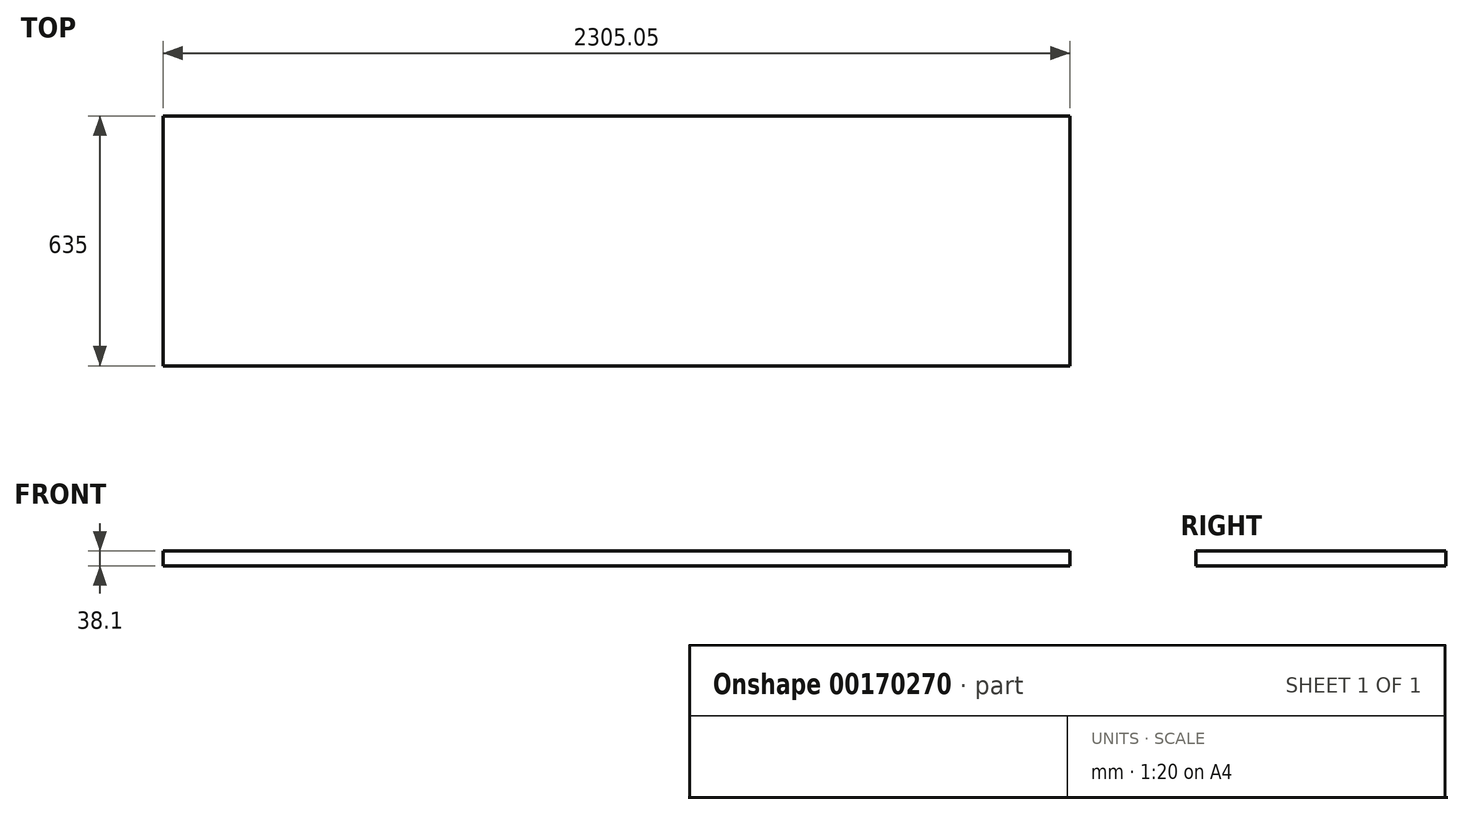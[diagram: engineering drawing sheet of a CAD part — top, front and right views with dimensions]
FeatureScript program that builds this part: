
annotation { "Feature Type Name" : "Feature", "Feature Type Description" : "" }
export const myFeature = defineFeature(function(context is Context, id is Id, definition is map)
    precondition{}
    {
        {
            var Q0;
            Q0=qCreatedBy(makeId("Top.planeOp"),FACE);
            var sketch = newSketch(context, id + "F0", { "sketchPlane" : qUnion([Q0])});
            skLineSegment(sketch, "E0", {"start": v(0, 0) * mm, "end": v(0, 635) * mm});
            skLineSegment(sketch, "E1", {"start": v(0, 635) * mm, "end": v(2305.05, 635) * mm});
            skLineSegment(sketch, "E2", {"start": v(2305.05, 635) * mm, "end": v(2305.05, 0) * mm});
            skLineSegment(sketch, "E3", {"start": v(2305.05, 0) * mm, "end": v(0, 0) * mm});
            skSolve(sketch);
        }
        {
            var Q0;
            Q0 = qSketchRegion(id + "F0", true);
            extrude(context, id + "F1", {"entities" : qUnion([Q0]), "depth" : 38.1 * mm});
        }
    });
